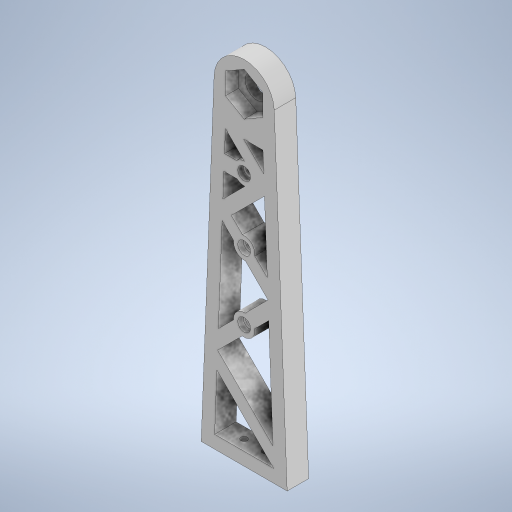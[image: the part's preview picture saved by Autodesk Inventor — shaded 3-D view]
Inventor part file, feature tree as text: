
AUTODESK INVENTOR PART (.ipt)
format: ipt  version: 2023 (Build 270158000, 158)  size: 490,496 bytes
history: native  units: mm
features: extrude x13, sketch x13, other x4, revolve x1, pattern_circular x1, mirror x1
ambient origin geometry x8: Origin, YZ Plane, XZ Plane, XY Plane, X Axis, Y Axis, Z Axis, Center Point
bodies: Body1 (feature_tree)
feature tree (33):
  other  "솔리드1"
  extrude  "돌출1"  Depth=66.0mm
  extrude  "돌출2"  Depth=10.0mm
  other  "작업 평면1"
  extrude  "돌출3"  Depth=10.0mm
  extrude  "돌출4"  Depth=30.0mm
  extrude  "돌출5"  Depth=50.0mm TaperAngle=0.0deg
  extrude  "돌출6"  Depth=28.0mm
  other  "작업 평면2"
  revolve  "회전1"
  extrude  "돌출7"  Depth=150.0mm
  extrude  "돌출8"  Depth=10.0mm TaperAngle=0.0deg
  pattern_circular  "원형 패턴1"  [2 undecoded]
  extrude  "돌출11"  Depth=6.0mm
  extrude  "돌출12"  Depth=6.0mm
  sketch  "스케치14"
  extrude  "돌출13"  Depth=10.0mm TaperAngle=0.0deg
  extrude  "돌출14"  Depth=6.0mm
  extrude  "돌출15"  TaperAngle=45.0deg  [1 undecoded]
  other  "작업 평면3"
  mirror  "미러1"
  sketch  "스케치1"
  sketch  "스케치2"
  sketch  "스케치3"
  sketch  "스케치4"
  sketch  "스케치5"
  sketch  "스케치6"
  sketch  "스케치7"
  sketch  "스케치8"
  sketch  "스케치9"
  sketch  "스케치12"
  sketch  "스케치13"
  sketch  "스케치15"
note: 3 required parameter values undecoded (feature->parameter linkage not recoverable at this tier; creation-order binding heuristic only, values carry confidence <= 0.55)
